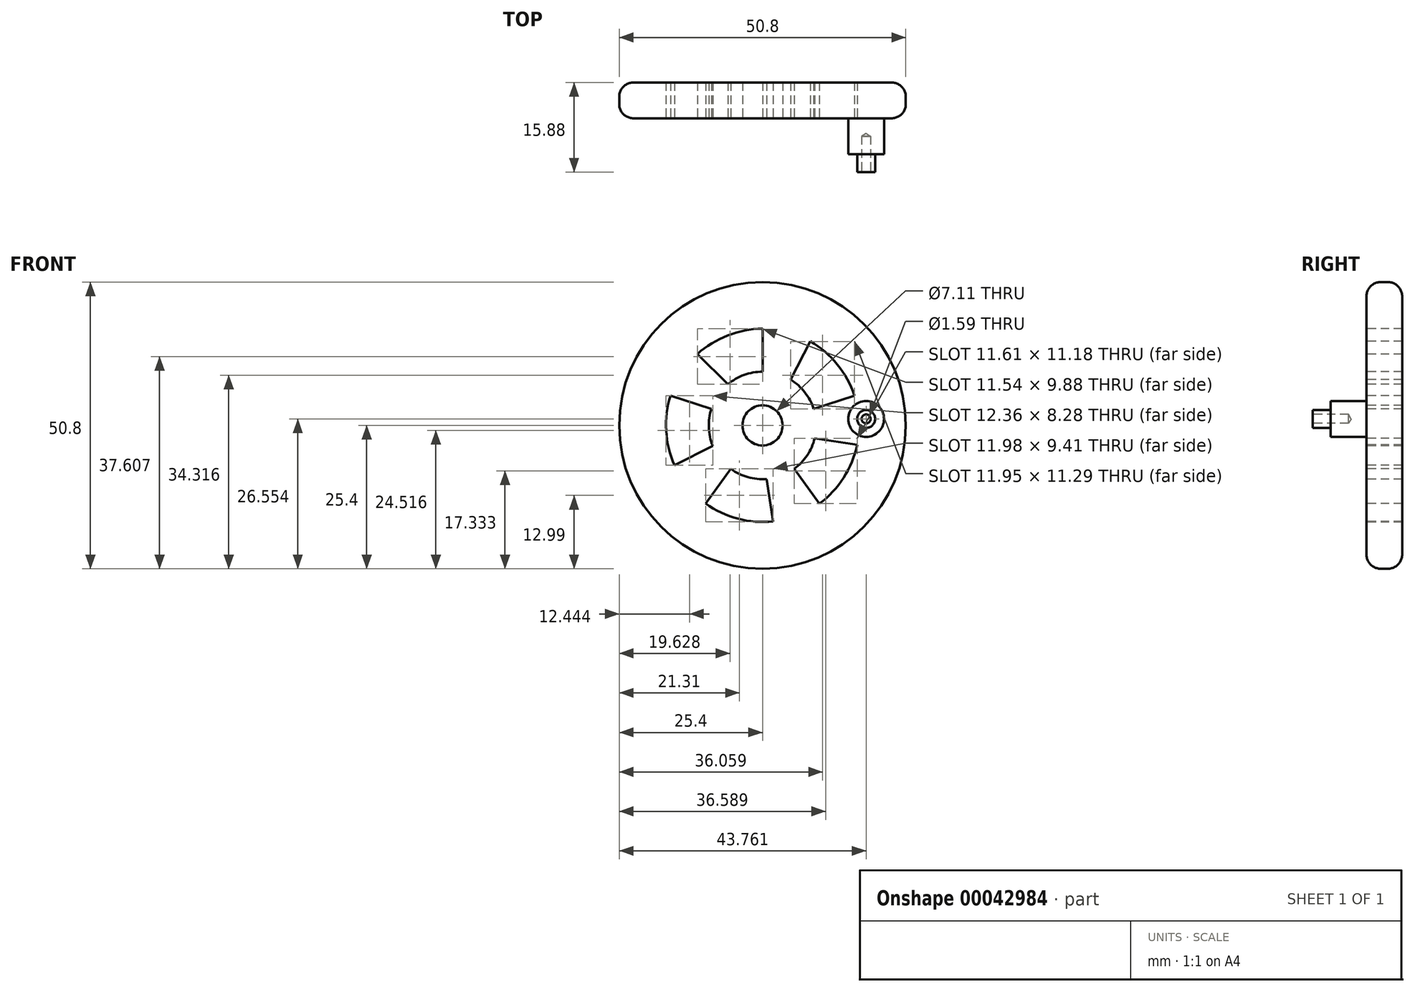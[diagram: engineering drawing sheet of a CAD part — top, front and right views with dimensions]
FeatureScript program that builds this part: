
annotation { "Feature Type Name" : "Feature", "Feature Type Description" : "" }
export const myFeature = defineFeature(function(context is Context, id is Id, definition is map)
    precondition{}
    {
        {
            var Q0;
            Q0=qCreatedBy(makeId("Front.planeOp"),FACE);
            var sketch = newSketch(context, id + "F0", { "sketchPlane" : qUnion([Q0])});
            skCircle(sketch, "E0", {"center": v(0, 0) * mm, "radius": 25.4 * mm});
            skSolve(sketch);
        }
        {
            var Q0;
            Q0=makeQuery(id+"F0.imprint","IMPRINT",FACE,{"disambiguationData":[TD([[makeQuery(id+"F0.imprint","IMPRINT",EDGE,{"derivedFrom":sQuery(id+"F0.wireOp",EDGE,"E0")}),1.0]])]});
            extrude(context, id + "F1", {"entities" : qUnion([Q0]), "depth" : 6.35 * mm});
        }
        {
            var Q0;
            Q0=makeQuery(id+"F1.opExtrude","CAP_EDGE",EDGE,{"disambiguationData":[OSD([sQuery(id+"F0.wireOp",EDGE,"E0")])],"isStart":false});
            var Q1;
            Q1=makeQuery(id+"F1.opExtrude","CAP_EDGE",EDGE,{"disambiguationData":[OSD([sQuery(id+"F0.wireOp",EDGE,"E0")])],"isStart":true});
            fillet(context, id + "F2", {"entities" : qUnion([Q0, Q1]), "radius" : 2.54 * mm, "tangentPropagation" : true, "allowEdgeOverflow" : false});
        }
        {
            var Q0;
            Q0=makeQuery(id+"F1.opExtrude","CAP_FACE",FACE,{"disambiguationData":[OSD([sQuery(id+"F0.wireOp",EDGE,"E0")])],"isStart":false});
            var sketch = newSketch(context, id + "F3", { "sketchPlane" : qUnion([Q0])});
            skCircle(sketch, "E1", {"center": v(0, 0) * mm, "radius": 9.53 * mm});
            skCircle(sketch, "E2", {"center": v(0, 0) * mm, "radius": 3.56 * mm});
            skLineSegment(sketch, "E3", {"start": v(0, 9.53) * mm, "end": v(0, 17.14) * mm});
            skLineSegment(sketch, "E4", {"start": v(-6.15, 7.27) * mm, "end": v(-11.54, 12.66) * mm});
            skArc(sketch, "E5", {"start": v(0, 17.14) * mm, "mid": v(-6.18, 15.95) * mm, "end": v(-11.54, 12.66) * mm});
            skArc(sketch, "E6.1.0", {"start": v(-16.3, 5.3) * mm, "mid": v(-17.08, -0.95) * mm, "end": v(-15.6, -7.07) * mm});
            skLineSegment(sketch, "E6.1.1", {"start": v(-8.82, -3.6) * mm, "end": v(-15.6, -7.07) * mm});
            skLineSegment(sketch, "E6.1.2", {"start": v(-9.06, 2.94) * mm, "end": v(-16.3, 5.3) * mm});
            skArc(sketch, "E6.2.0", {"start": v(-10.08, -13.87) * mm, "mid": v(-4.38, -16.53) * mm, "end": v(1.9, -17.02) * mm});
            skLineSegment(sketch, "E6.2.1", {"start": v(0.7, -9.5) * mm, "end": v(1.9, -17.02) * mm});
            skLineSegment(sketch, "E6.2.2", {"start": v(-5.6, -7.7) * mm, "end": v(-10.08, -13.87) * mm});
            skArc(sketch, "E6.3.0", {"start": v(10.08, -13.87) * mm, "mid": v(14.37, -9.27) * mm, "end": v(16.78, -3.46) * mm});
            skLineSegment(sketch, "E6.3.1", {"start": v(9.25, -2.26) * mm, "end": v(16.78, -3.46) * mm});
            skLineSegment(sketch, "E6.3.2", {"start": v(5.6, -7.7) * mm, "end": v(10.08, -13.87) * mm});
            skArc(sketch, "E6.4.0", {"start": v(16.3, 5.3) * mm, "mid": v(13.26, 10.8) * mm, "end": v(8.47, 14.89) * mm});
            skLineSegment(sketch, "E6.4.1", {"start": v(5.01, 8.1) * mm, "end": v(8.47, 14.89) * mm});
            skLineSegment(sketch, "E6.4.2", {"start": v(9.06, 2.94) * mm, "end": v(16.3, 5.3) * mm});
            skSolve(sketch);
        }
        {
            var Q0;
            {var subQ1=sQuery(id+"F3.wireOp",EDGE,"E3");Q0=makeQuery(id+"F3.imprint","IMPRINT",FACE,{"disambiguationData":[TD([[makeQuery(id+"F3.imprint","IMPRINT",EDGE,{"derivedFrom":subQ1}),1.0]])]});}
            var Q1;
            Q1=makeQuery(id+"F3.imprint","IMPRINT",FACE,{"disambiguationData":[TD([[makeQuery(id+"F3.imprint","IMPRINT",EDGE,{"derivedFrom":sQuery(id+"F3.wireOp",EDGE,"E6.1.0")}),1.0]])]});
            var Q2;
            Q2=makeQuery(id+"F3.imprint","IMPRINT",FACE,{"disambiguationData":[TD([[makeQuery(id+"F3.imprint","IMPRINT",EDGE,{"derivedFrom":sQuery(id+"F3.wireOp",EDGE,"E6.2.0")}),1.0]])]});
            var Q3;
            Q3=makeQuery(id+"F3.imprint","IMPRINT",FACE,{"disambiguationData":[TD([[makeQuery(id+"F3.imprint","IMPRINT",EDGE,{"derivedFrom":sQuery(id+"F3.wireOp",EDGE,"E6.3.0")}),1.0]])]});
            var Q4;
            Q4=makeQuery(id+"F3.imprint","IMPRINT",FACE,{"disambiguationData":[TD([[makeQuery(id+"F3.imprint","IMPRINT",EDGE,{"derivedFrom":sQuery(id+"F3.wireOp",EDGE,"E6.4.0")}),1.0]])]});
            extrude(context, id + "F4", {"entities" : qUnion([Q0, Q1, Q2, Q3, Q4]), "operationType" : NewBodyOperationType.REMOVE, "oppositeDirection" : true, "depth" : 6.35 * mm});
        }
        {
            var Q0;
            Q0=makeQuery(id+"F1.opExtrude","CAP_FACE",FACE,{"disambiguationData":[OSD([sQuery(id+"F0.wireOp",EDGE,"E0")])],"isStart":false});
            var sketch = newSketch(context, id + "F5", { "sketchPlane" : qUnion([Q0])});
            skCircle(sketch, "E7", {"center": v(0, 0) * mm, "radius": 4.7 * mm});
            skSolve(sketch);
        }
        {
            var Q0;
            Q0=sQuery(id+"F5.wireOp",VERTEX,"E7.center");
            var Q1;
            Q1=makeQuery(id+"F1.opExtrude","SWEPT_BODY",BODY,{"disambiguationData":[OSD([sQuery(id+"F0.wireOp",EDGE,"E0")])]});
            hole(context, id + "F6", {"style" : HoleStyle.SIMPLE, "holeDiameter" : 7.11 * mm, "endStyle" : HoleEndStyle.THROUGH, "locations" : qUnion([Q0]), "scope" : qUnion([Q1])});
        }
        {
            var Q0;
            Q0=makeQuery(id+"F1.opExtrude","CAP_FACE",FACE,{"disambiguationData":[OSD([sQuery(id+"F0.wireOp",EDGE,"E0")])],"isStart":false});
            var sketch = newSketch(context, id + "F7", { "sketchPlane" : qUnion([Q0])});
            skCircle(sketch, "E8", {"center": v(18.36, 1.15) * mm, "radius": 3.18 * mm});
            skSolve(sketch);
        }
        {
            var Q0;
            Q0=makeQuery(id+"F7.imprint","IMPRINT",FACE,{"disambiguationData":[TD([[makeQuery(id+"F7.imprint","IMPRINT",EDGE,{"derivedFrom":sQuery(id+"F7.wireOp",EDGE,"E8")}),1.0]])]});
            extrude(context, id + "F8", {"entities" : qUnion([Q0]), "operationType" : NewBodyOperationType.ADD, "depth" : 6.35 * mm});
        }
        {
            var Q0;
            Q0=makeQuery(id+"F8.opExtrude","CAP_FACE",FACE,{"disambiguationData":[OSD([sQuery(id+"F7.wireOp",EDGE,"E8")])],"isStart":false});
            var sketch = newSketch(context, id + "F9", { "sketchPlane" : qUnion([Q0])});
            skCircle(sketch, "E9", {"center": v(18.36, 1.15) * mm, "radius": 1.59 * mm});
            skSolve(sketch);
        }
        {
            var Q0;
            Q0=makeQuery(id+"F9.imprint","IMPRINT",FACE,{"disambiguationData":[TD([[makeQuery(id+"F9.imprint","IMPRINT",EDGE,{"derivedFrom":sQuery(id+"F9.wireOp",EDGE,"E9")}),1.0]])]});
            extrude(context, id + "F10", {"entities" : qUnion([Q0]), "operationType" : NewBodyOperationType.ADD, "depth" : 3.17 * mm});
        }
        {
            var Q0;
            Q0=makeQuery(id+"F10.opExtrude","CAP_FACE",FACE,{"disambiguationData":[OSD([sQuery(id+"F9.wireOp",EDGE,"E9")])],"isStart":false});
            var sketch = newSketch(context, id + "F11", { "sketchPlane" : qUnion([Q0])});
            skCircle(sketch, "E10", {"center": v(18.36, 1.15) * mm, "radius": 0.84 * mm});
            skSolve(sketch);
        }
        {
            var Q0;
            Q0=sQuery(id+"F11.wireOp",VERTEX,"E10.center");
            var Q1;
            Q1=makeQuery(id+"F1.opExtrude","SWEPT_BODY",BODY,{"disambiguationData":[OSD([sQuery(id+"F0.wireOp",EDGE,"E0")])]});
            hole(context, id + "F12", {"style" : HoleStyle.SIMPLE, "holeDiameter" : 1.59 * mm, "endStyle" : HoleEndStyle.BLIND, "holeDepth" : 6.35 * mm, "locations" : qUnion([Q0]), "scope" : qUnion([Q1])});
        }
    });
